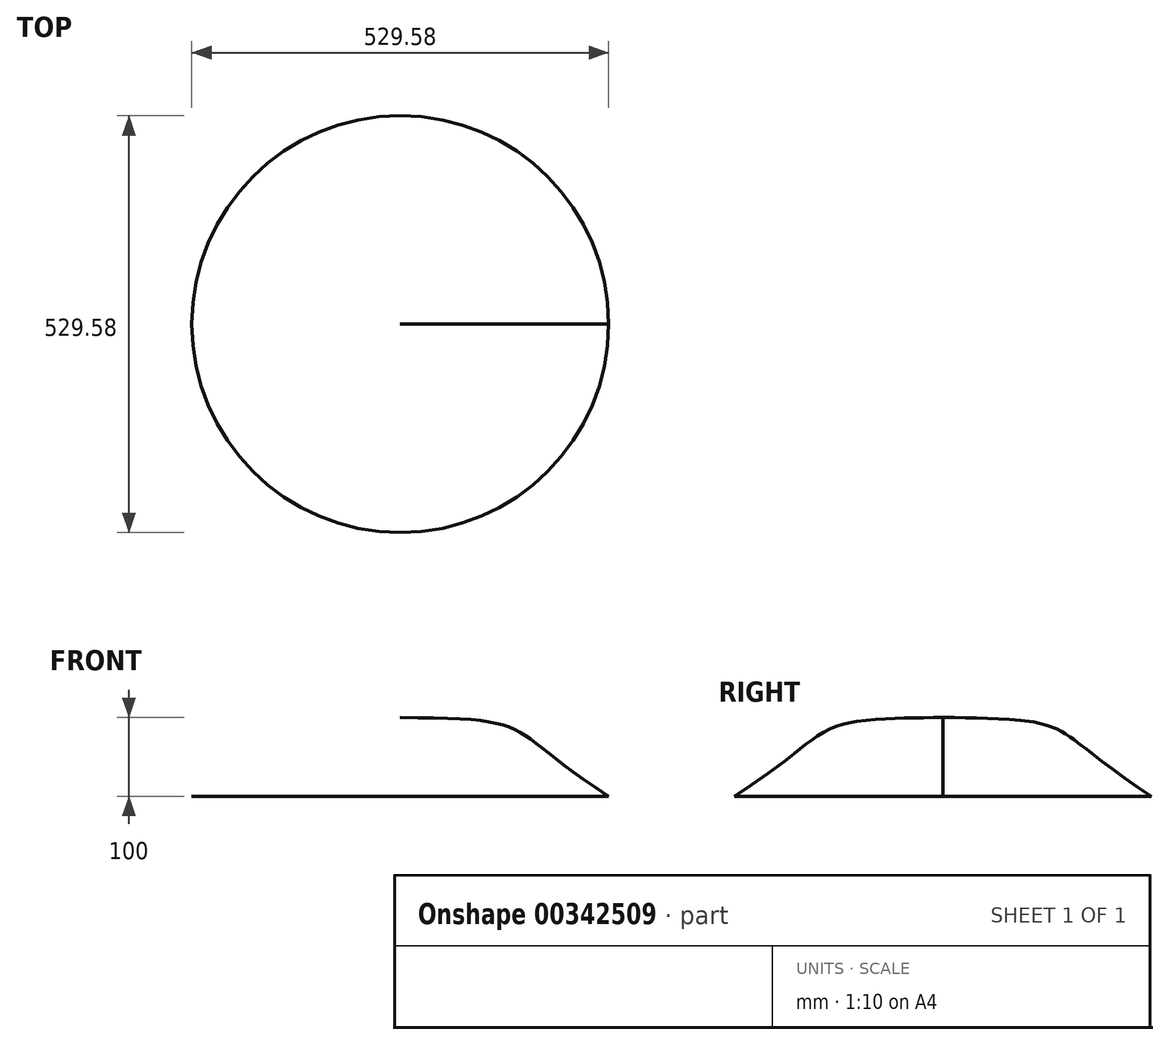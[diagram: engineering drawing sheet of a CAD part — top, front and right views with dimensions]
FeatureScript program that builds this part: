
annotation { "Feature Type Name" : "Feature", "Feature Type Description" : "" }
export const myFeature = defineFeature(function(context is Context, id is Id, definition is map)
    precondition{}
    {
        {
            var Q0;
            Q0=qCreatedBy(makeId("Front.planeOp"),FACE);
            var sketch = newSketch(context, id + "F0", { "sketchPlane" : qUnion([Q0])});
            skLineSegment(sketch, "E0", {"start": v(0, 0) * mm, "end": v(264.79, 0) * mm});
            skLineSegment(sketch, "E1", {"start": v(0, 0) * mm, "end": v(0, 100) * mm});
            skFitSpline(sketch, "E2", {"points": [v(0, 100) * mm, v(264.79, 0) * mm], "startDerivative": vector(547.81, -3.67) * mm, "endDerivative": vector(418.53, -269.07) * mm});
            skSolve(sketch);
        }
        {
            var Q0;
            Q0 = qSketchRegion(id + "F0", true);
            var Q1;
            Q1=sQuery(id+"F0.wireOp",EDGE,"E1");
            revolve(context, id + "F1", {"entities" : qUnion([Q0]), "axis" : qUnion([Q1]), "revolveType" : RevolveType.FULL});
        }
    });
